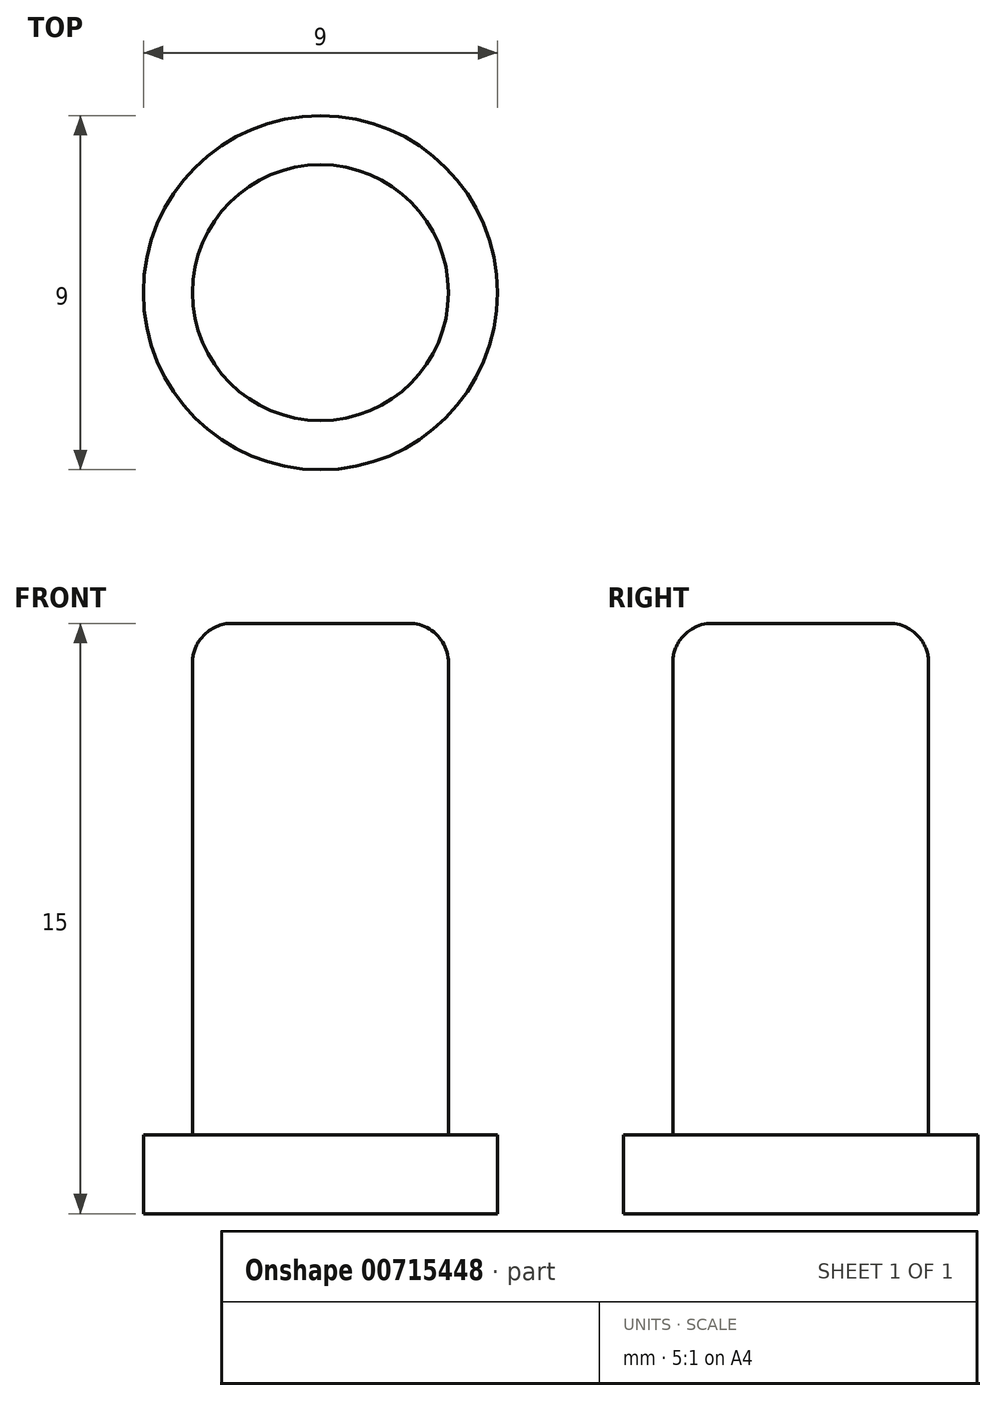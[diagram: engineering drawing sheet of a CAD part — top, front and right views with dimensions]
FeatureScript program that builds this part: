
annotation { "Feature Type Name" : "Feature", "Feature Type Description" : "" }
export const myFeature = defineFeature(function(context is Context, id is Id, definition is map)
    precondition{}
    {
        {
            var Q0;
            Q0=qCreatedBy(makeId("Top.planeOp"),FACE);
            var sketch = newSketch(context, id + "F0", { "sketchPlane" : qUnion([Q0])});
            skCircle(sketch, "E0", {"center": v(-22.53, 0) * mm, "radius": 4.5 * mm});
            skCircle(sketch, "E1", {"center": v(-22.53, 0) * mm, "radius": 3.25 * mm});
            skSolve(sketch);
        }
        {
            var Q0;
            Q0=makeQuery(id+"F0.imprint","IMPRINT",FACE,{"disambiguationData":[TD([[makeQuery(id+"F0.imprint","IMPRINT",EDGE,{"derivedFrom":sQuery(id+"F0.wireOp",EDGE,"E1")}),1.0]])]});
            extrude(context, id + "F1", {"entities" : qUnion([Q0]), "depth" : 13 * mm, "offsetDistance" : 25 * mm});
        }
        {
            var Q0;
            Q0=makeQuery(id+"F0.imprint","IMPRINT",FACE,{"disambiguationData":[TD([[makeQuery(id+"F0.imprint","IMPRINT",EDGE,{"derivedFrom":sQuery(id+"F0.wireOp",EDGE,"E0")}),1.0]])]});
            var Q1;
            Q1=makeQuery(id+"F0.imprint","IMPRINT",FACE,{"disambiguationData":[TD([[makeQuery(id+"F0.imprint","IMPRINT",EDGE,{"derivedFrom":sQuery(id+"F0.wireOp",EDGE,"E1")}),1.0]])]});
            extrude(context, id + "F2", {"entities" : qUnion([Q0, Q1]), "operationType" : NewBodyOperationType.ADD, "oppositeDirection" : true, "depth" : 2 * mm, "offsetDistance" : 25 * mm});
        }
        {
            var Q0;
            Q0=makeQuery(id+"F1.opExtrude","CAP_EDGE",EDGE,{"disambiguationData":[OSD([sQuery(id+"F0.wireOp",EDGE,"E1")])],"isStart":false});
            fillet(context, id + "F3", {"entities" : qUnion([Q0]), "tangentPropagation" : true, "radius" : 1 * mm, "defaultsChanged" : true, "vertexSettings" : [], "allowEdgeOverflow" : false});
        }
    });
